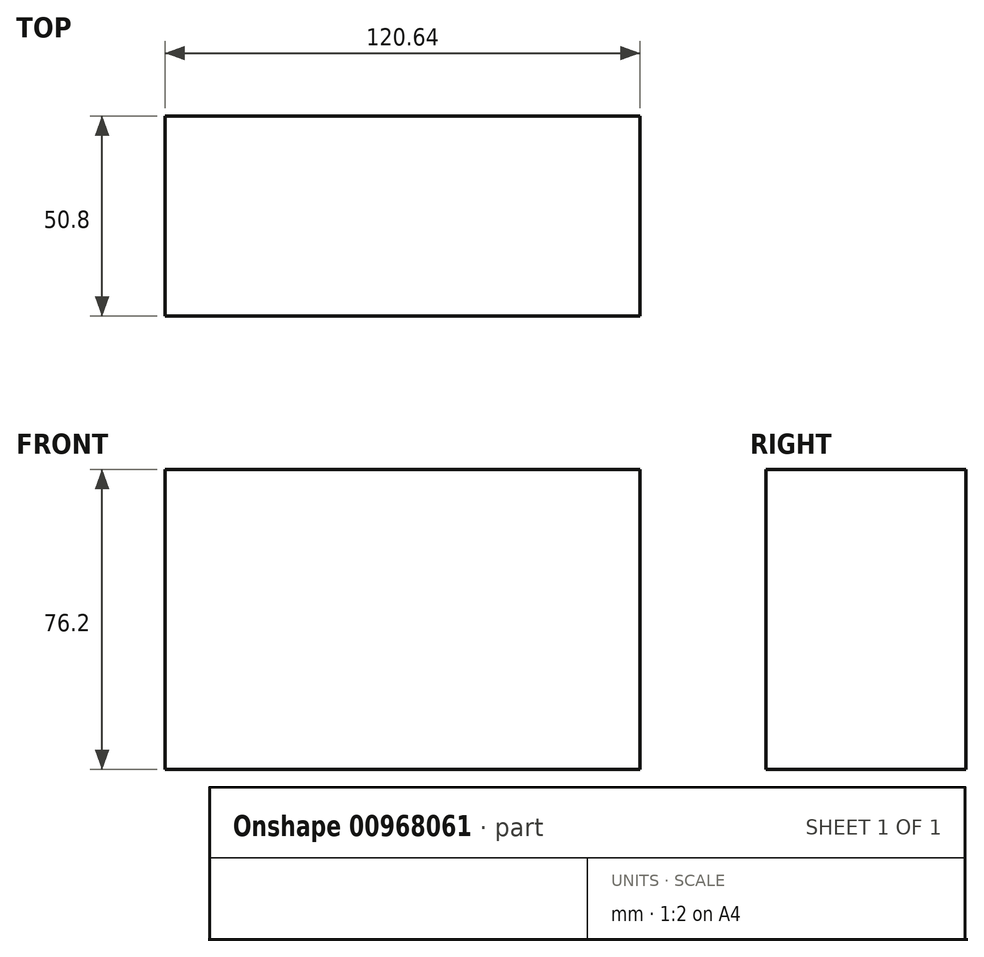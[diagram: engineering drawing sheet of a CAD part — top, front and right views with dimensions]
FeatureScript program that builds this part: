
annotation { "Feature Type Name" : "Feature", "Feature Type Description" : "" }
export const myFeature = defineFeature(function(context is Context, id is Id, definition is map)
    precondition{}
    {
        {
            var Q0;
            Q0=qCreatedBy(makeId("Front.planeOp"),FACE);
            var sketch = newSketch(context, id + "F0", { "sketchPlane" : qUnion([Q0])});
            skLineSegment(sketch, "E0.bottom", {"start": v(60.33, 38.1) * mm, "end": v(-60.33, 38.1) * mm});
            skLineSegment(sketch, "E0.top", {"start": v(60.33, -38.1) * mm, "end": v(-60.33, -38.1) * mm});
            skLineSegment(sketch, "E0.left", {"start": v(60.33, 38.1) * mm, "end": v(60.33, -38.1) * mm});
            skLineSegment(sketch, "E0.right", {"start": v(-60.33, 38.1) * mm, "end": v(-60.33, -38.1) * mm});
            skPoint(sketch, "E0.middle", {"position": v(0, 0) * mm});
            skSolve(sketch);
        }
        {
            var Q0;
            Q0 = qSketchRegion(id + "F0", true);
            extrude(context, id + "F1", {"entities" : qUnion([Q0]), "endBound" : BoundingType.SYMMETRIC, "depth" : 50.8 * mm, "offsetDistance" : 25.4 * mm});
        }
    });
